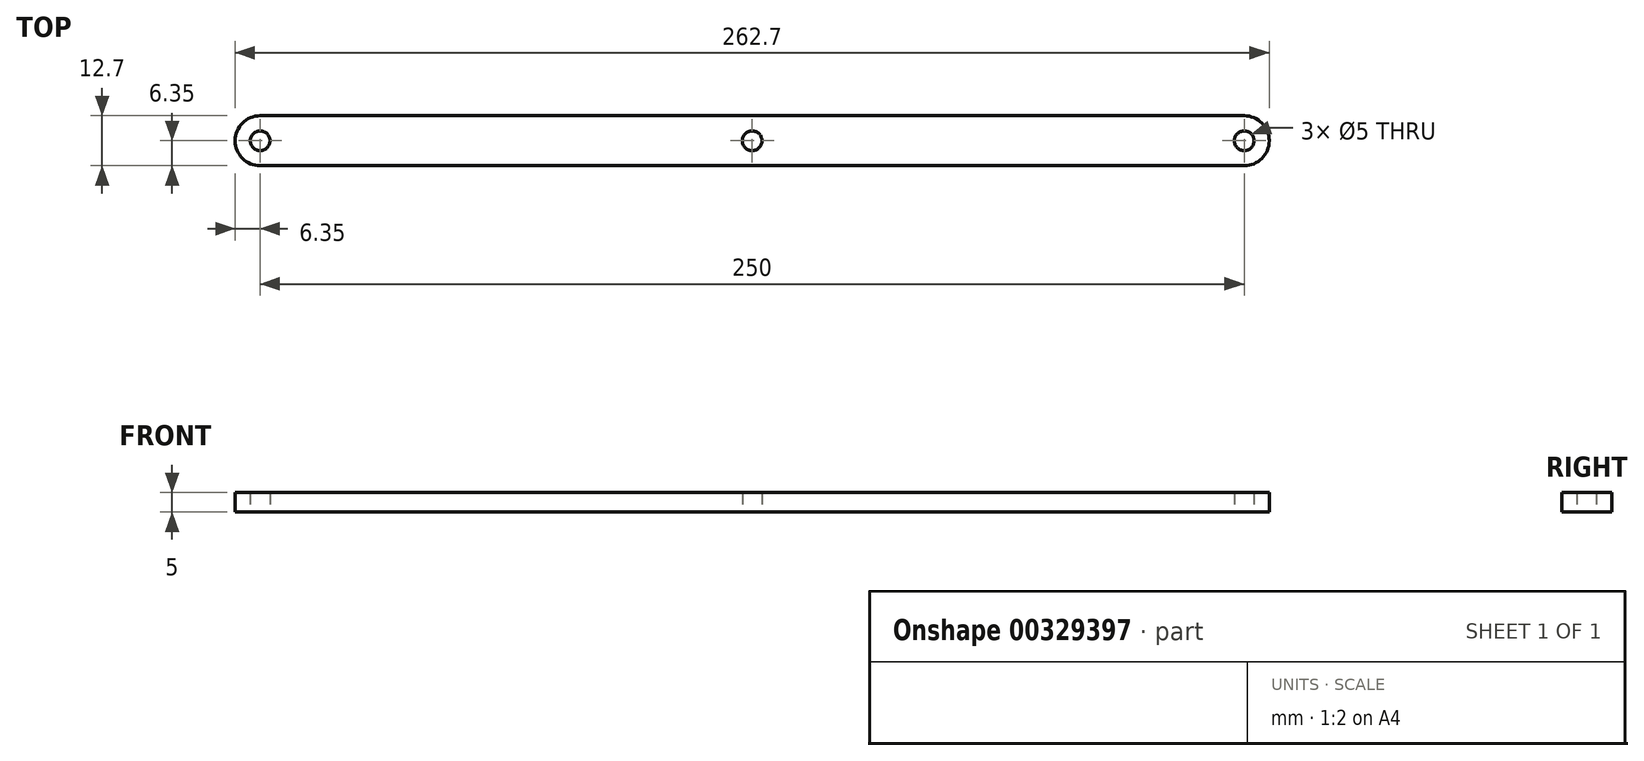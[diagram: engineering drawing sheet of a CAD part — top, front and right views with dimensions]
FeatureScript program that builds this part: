
annotation { "Feature Type Name" : "Feature", "Feature Type Description" : "" }
export const myFeature = defineFeature(function(context is Context, id is Id, definition is map)
    precondition{}
    {
        {
            var Q0;
            Q0=qCreatedBy(makeId("Top.planeOp"),FACE);
            var sketch = newSketch(context, id + "F0", { "sketchPlane" : qUnion([Q0])});
            skLineSegment(sketch, "E0.bottom", {"start": v(125, -6.35) * mm, "end": v(-125, -6.35) * mm});
            skLineSegment(sketch, "E0.top", {"start": v(125, 6.35) * mm, "end": v(-125, 6.35) * mm});
            skPoint(sketch, "E0.middle", {"position": v(0, 0) * mm});
            skArc(sketch, "E1", {"start": v(-125, 6.35) * mm, "mid": v(-131.35, 0) * mm, "end": v(-125, -6.35) * mm});
            skArc(sketch, "E2", {"start": v(125, -6.35) * mm, "mid": v(131.35, 0) * mm, "end": v(125, 6.35) * mm});
            skCircle(sketch, "E3", {"center": v(-125, 0) * mm, "radius": 2.5 * mm});
            skCircle(sketch, "E4", {"center": v(125, 0) * mm, "radius": 2.5 * mm});
            skCircle(sketch, "E5", {"center": v(0, 0) * mm, "radius": 2.5 * mm});
            skSolve(sketch);
        }
        {
            var Q0;
            Q0=makeQuery(id+"F0.imprint","IMPRINT",FACE,{"disambiguationData":[TD([[makeQuery(id+"F0.imprint","IMPRINT",EDGE,{"derivedFrom":sQuery(id+"F0.wireOp",EDGE,"E0.bottom")}),-1.0]])]});
            extrude(context, id + "F1", {"entities" : qUnion([Q0]), "depth" : 5 * mm});
        }
    });
